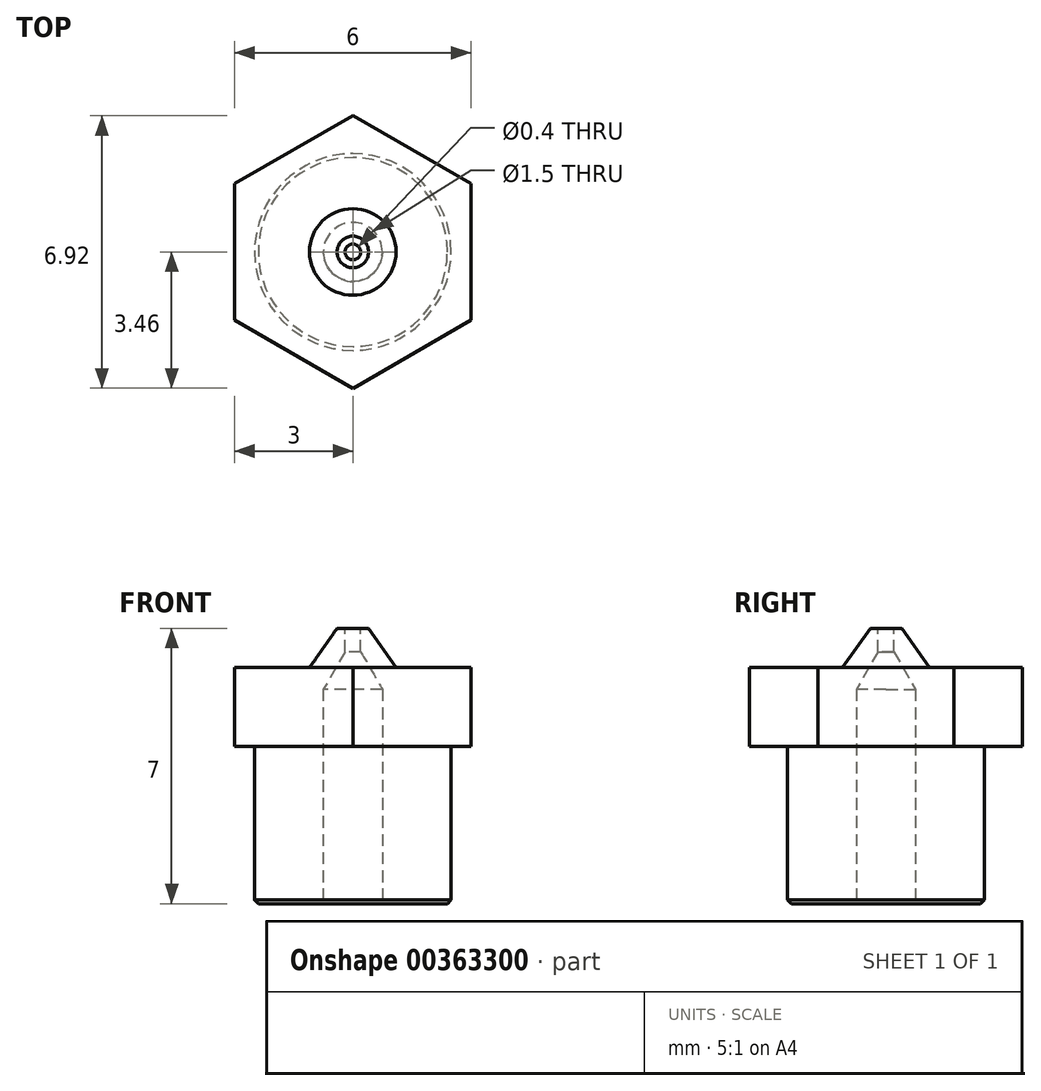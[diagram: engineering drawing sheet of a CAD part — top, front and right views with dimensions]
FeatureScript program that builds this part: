
annotation { "Feature Type Name" : "Feature", "Feature Type Description" : "" }
export const myFeature = defineFeature(function(context is Context, id is Id, definition is map)
    precondition{}
    {
        {
            var Q0;
            Q0=qCreatedBy(makeId("Top.planeOp"),FACE);
            var sketch = newSketch(context, id + "F10", { "sketchPlane" : qUnion([Q0])});
            skCircle(sketch, "E0.cCircle", {"center": v(0, 0) * mm, "radius": 3.46 * mm, "construction": true});
            skLineSegment(sketch, "E0.0", {"start": v(3, -1.73) * mm, "end": v(0, -3.46) * mm});
            skLineSegment(sketch, "E0.1", {"start": v(0, -3.46) * mm, "end": v(-3, -1.73) * mm});
            skLineSegment(sketch, "E0.2", {"start": v(-3, -1.73) * mm, "end": v(-3, 1.73) * mm});
            skLineSegment(sketch, "E0.3", {"start": v(-3, 1.73) * mm, "end": v(0, 3.46) * mm});
            skLineSegment(sketch, "E0.4", {"start": v(0, 3.46) * mm, "end": v(3, 1.73) * mm});
            skLineSegment(sketch, "E0.5", {"start": v(3, 1.73) * mm, "end": v(3, -1.73) * mm});
            skLineSegment(sketch, "E1", {"start": v(0, 0) * mm, "end": v(0, 3.46) * mm, "construction": true});
            skSolve(sketch);
        }
        {
            var Q0;
            Q0=makeQuery(id+"F10.imprint","IMPRINT",FACE,{"disambiguationData":[TD([[makeQuery(id+"F10.imprint","IMPRINT",EDGE,{"derivedFrom":sQuery(id+"F10.wireOp",EDGE,"E0.0")}),-1.0]])]});
            extrude(context, id + "F0", {"entities" : qUnion([Q0]), "depth" : 2 * mm});
        }
        {
            var Q0;
            Q0=qCreatedBy(makeId("Origin.pointOp"),VERTEX);
            var Q1;
            Q1=makeQuery(id+"F0.opExtrude","CAP_VERTEX",VERTEX,{"disambiguationData":[OSD([sQuery(id+"F10.wireOp",EDGE,"E0.0"),sQuery(id+"F10.wireOp",EDGE,"E0.1")])],"isStart":false});
            var Q2;
            Q2=makeQuery(id+"F0.opExtrude","CAP_VERTEX",VERTEX,{"disambiguationData":[OSD([sQuery(id+"F10.wireOp",EDGE,"E0.3"),sQuery(id+"F10.wireOp",EDGE,"E0.4")])],"isStart":true});
            cPlane(context, id + "F1", {"entities" : qUnion([Q0, Q1, Q2]), "cplaneType" : CPlaneType.THREE_POINT, "offset" : 25 * mm, "width" : 150 * mm, "height" : 150 * mm});
        }
        {
            var Q0;
            Q0=qCreatedBy(makeId("Right.planeOp"),FACE);
            var sketch = newSketch(context, id + "F2", { "sketchPlane" : qUnion([Q0])});
            skLineSegment(sketch, "E2", {"start": v(0, 0) * mm, "end": v(0, 3.8) * mm, "construction": true});
            skLineSegment(sketch, "E3", {"start": v(0, 3) * mm, "end": v(0, 2) * mm});
            skLineSegment(sketch, "E4", {"start": v(0, 2) * mm, "end": v(-1.1, 2) * mm});
            skLineSegment(sketch, "E5", {"start": v(-1.1, 2) * mm, "end": v(-0.4, 3) * mm});
            skLineSegment(sketch, "E6", {"start": v(-0.4, 3) * mm, "end": v(0, 3) * mm});
            skSolve(sketch);
        }
        {
            var Q0;
            Q0=makeQuery(id+"F2.imprint","IMPRINT",FACE,{"disambiguationData":[TD([[makeQuery(id+"F2.imprint","IMPRINT",EDGE,{"derivedFrom":sQuery(id+"F2.wireOp",EDGE,"E3")}),-1.0]])]});
            var Q1;
            Q1=sQuery(id+"F2.wireOp",EDGE,"E2");
            revolve(context, id + "F11", {"operationType" : NewBodyOperationType.ADD, "entities" : qUnion([Q0]), "axis" : qUnion([Q1]), "revolveType" : RevolveType.FULL});
        }
        {
            var Q0;
            Q0=makeQuery(id+"F0.opExtrude","CAP_FACE",FACE,{"disambiguationData":[OSD([sQuery(id+"F10.wireOp",EDGE,"E0.0"),sQuery(id+"F10.wireOp",EDGE,"E0.1"),sQuery(id+"F10.wireOp",EDGE,"E0.2"),sQuery(id+"F10.wireOp",EDGE,"E0.3"),sQuery(id+"F10.wireOp",EDGE,"E0.4"),sQuery(id+"F10.wireOp",EDGE,"E0.5")])],"isStart":true});
            var sketch = newSketch(context, id + "F12", { "sketchPlane" : qUnion([Q0])});
            skCircle(sketch, "E7", {"center": v(0, 0) * mm, "radius": 2.5 * mm});
            skSolve(sketch);
        }
        {
            var Q0;
            Q0=makeQuery(id+"F12.imprint","IMPRINT",FACE,{"disambiguationData":[TD([[makeQuery(id+"F12.imprint","IMPRINT",EDGE,{"derivedFrom":sQuery(id+"F12.wireOp",EDGE,"E7")}),1.0]])]});
            extrude(context, id + "F13", {"entities" : qUnion([Q0]), "operationType" : NewBodyOperationType.ADD, "depth" : 4 * mm});
        }
        {
            var Q0;
            Q0=makeQuery(id+"F13.opExtrude","CAP_EDGE",EDGE,{"disambiguationData":[OSD([sQuery(id+"F12.wireOp",EDGE,"E7")])],"isStart":false});
            chamfer(context, id + "F3", {"entities" : qUnion([Q0]), "width" : 0.1 * mm, "tangentPropagation" : true});
        }
        {
            var Q0;
            Q0=makeQuery(id+"F11.opRevolve","SWEPT_FACE",FACE,{"disambiguationData":[OSD([sQuery(id+"F2.wireOp",EDGE,"E6")])]});
            var sketch = newSketch(context, id + "F4", { "sketchPlane" : qUnion([Q0])});
            skCircle(sketch, "E8", {"center": v(0, 0) * mm, "radius": 0.2 * mm});
            skSolve(sketch);
        }
        {
            var Q0;
            Q0=makeQuery(id+"F4.imprint","IMPRINT",FACE,{"disambiguationData":[TD([[makeQuery(id+"F4.imprint","IMPRINT",EDGE,{"derivedFrom":sQuery(id+"F4.wireOp",EDGE,"E8")}),1.0]])]});
            extrude(context, id + "F5", {"entities" : qUnion([Q0]), "operationType" : NewBodyOperationType.REMOVE, "oppositeDirection" : true, "depth" : 0.6 * mm});
        }
        {
            var Q0;
            Q0=qCreatedBy(id+"F1.planeOp",FACE);
            var sketch = newSketch(context, id + "F6", { "sketchPlane" : qUnion([Q0])});
            skLineSegment(sketch, "E9", {"start": v(0, 2.4) * mm, "end": v(-0.2, 2.4) * mm});
            skLineSegment(sketch, "E10", {"start": v(-0.2, 2.4) * mm, "end": v(-0.75, 1.45) * mm});
            skLineSegment(sketch, "E11", {"start": v(-0.75, 1.45) * mm, "end": v(0, 1.45) * mm});
            skLineSegment(sketch, "E12", {"start": v(0, 1.45) * mm, "end": v(0, 2.4) * mm});
            skSolve(sketch);
        }
        {
            var Q0;
            Q0=qSketchRegion(id+"F6",true);
            var Q1;
            Q1=sQuery(id+"F6.wireOp",EDGE,"E12");
            revolve(context, id + "F7", {"operationType" : NewBodyOperationType.REMOVE, "entities" : qUnion([Q0]), "axis" : qUnion([Q1]), "revolveType" : RevolveType.FULL, "oppositeDirection" : true});
        }
        {
            var Q0;
            Q0=makeQuery(id+"F13.opExtrude","CAP_FACE",FACE,{"disambiguationData":[OSD([sQuery(id+"F12.wireOp",EDGE,"E7")])],"isStart":false});
            var sketch = newSketch(context, id + "F8", { "sketchPlane" : qUnion([Q0])});
            skCircle(sketch, "E13", {"center": v(0, 0) * mm, "radius": 0.75 * mm});
            skSolve(sketch);
        }
        {
            var Q0;
            Q0=makeQuery(id+"F8.imprint","IMPRINT",FACE,{"disambiguationData":[TD([[makeQuery(id+"F8.imprint","IMPRINT",EDGE,{"derivedFrom":sQuery(id+"F8.wireOp",EDGE,"E13")}),1.0]])]});
            extrude(context, id + "F9", {"entities" : qUnion([Q0]), "operationType" : NewBodyOperationType.REMOVE, "oppositeDirection" : true, "depth" : 5.45 * mm});
        }
    });
